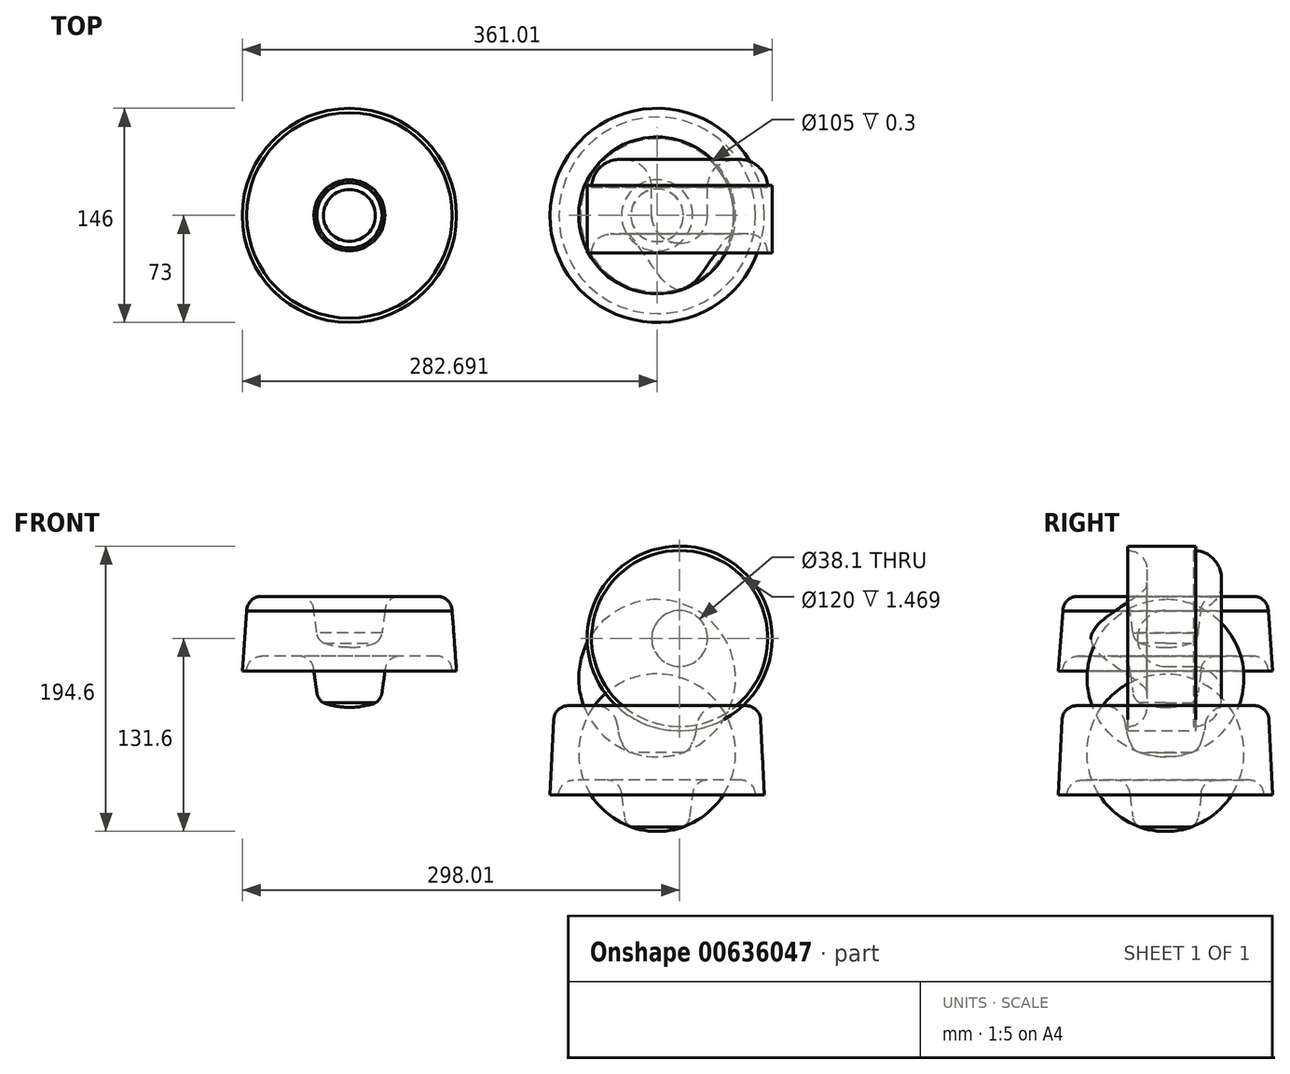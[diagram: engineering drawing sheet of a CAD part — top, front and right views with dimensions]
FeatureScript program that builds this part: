
annotation { "Feature Type Name" : "Feature", "Feature Type Description" : "" }
export const myFeature = defineFeature(function(context is Context, id is Id, definition is map)
    precondition{}
    {
        {
            var Q0;
            Q0=qCreatedBy(makeId("Top.planeOp"),FACE);
            var sketch = newSketch(context, id + "F0", { "sketchPlane" : qUnion([Q0])});
            skLineSegment(sketch, "E0", {"start": v(-19.05, 19.05) * mm, "end": v(19.05, 19.05) * mm, "construction": true});
            skPoint(sketch, "E1", {"position": v(0, 19.05) * mm});
            skLineSegment(sketch, "E2", {"start": v(19.05, 19.05) * mm, "end": v(19.05, 0) * mm});
            skLineSegment(sketch, "E3", {"start": v(-19.05, 19.05) * mm, "end": v(-19.05, 0) * mm});
            skArc(sketch, "E4", {"start": v(-19.05, 0) * mm, "mid": v(0, -19.05) * mm, "end": v(19.05, 0) * mm});
            skLineSegment(sketch, "E5", {"start": v(-19.05, 19.05) * mm, "end": v(-19.05, 19.05) * mm});
            skLineSegment(sketch, "E6", {"start": v(-38.1, 38.1) * mm, "end": v(-40.95, 38.1) * mm});
            skLineSegment(sketch, "E7", {"start": v(-60, 20.52) * mm, "end": v(-60, 19.05) * mm});
            skLineSegment(sketch, "E8", {"start": v(-60, 20.52) * mm, "end": v(-63, 20.52) * mm});
            skLineSegment(sketch, "E9", {"start": v(-63, 20.52) * mm, "end": v(-63, -25.7) * mm});
            skLineSegment(sketch, "E10", {"start": v(-63, -25.7) * mm, "end": v(-60, -25.7) * mm});
            skLineSegment(sketch, "E11", {"start": v(-60, -25.7) * mm, "end": v(-60, -25.7) * mm});
            skPoint(sketch, "E12.visualSharp", {"position": v(-60, 38.1) * mm});
            skArc(sketch, "E12.filletArc", {"start": v(-40.95, 38.1) * mm, "mid": v(-54.42, 32.52) * mm, "end": v(-60, 19.05) * mm});
            skPoint(sketch, "E13.visualSharp", {"position": v(-19.05, 38.1) * mm});
            skArc(sketch, "E13.filletArc", {"start": v(-19.05, 19.05) * mm, "mid": v(-24.63, 32.52) * mm, "end": v(-38.1, 38.1) * mm});
            skLineSegment(sketch, "E14", {"start": v(-47, -12.7) * mm, "end": v(-38.1, -12.7) * mm});
            skPoint(sketch, "E15.visualSharp", {"position": v(-60, -12.7) * mm});
            skArc(sketch, "E15.filletArc", {"start": v(-47, -12.7) * mm, "mid": v(-56.2, -16.5) * mm, "end": v(-60, -25.7) * mm});
            skLineSegment(sketch, "E16", {"start": v(0, 0) * mm, "end": v(0, -8.3) * mm, "construction": true});
            skLineSegment(sketch, "E17.MirrorCS", {"start": v(47, -12.7) * mm, "end": v(38.1, -12.7) * mm});
            skArc(sketch, "E18.MirrorCS", {"start": v(47, -12.7) * mm, "mid": v(56.2, -16.5) * mm, "end": v(60, -25.7) * mm});
            skLineSegment(sketch, "E19.MirrorCS", {"start": v(60, -25.7) * mm, "end": v(60, -25.7) * mm});
            skLineSegment(sketch, "E20.MirrorCS", {"start": v(63, -25.7) * mm, "end": v(60, -25.7) * mm});
            skLineSegment(sketch, "E21.MirrorCS", {"start": v(63, 20.52) * mm, "end": v(63, -25.7) * mm});
            skLineSegment(sketch, "E22.MirrorCS", {"start": v(60, 20.52) * mm, "end": v(63, 20.52) * mm});
            skArc(sketch, "E23.MirrorCS", {"start": v(40.95, 38.1) * mm, "mid": v(54.42, 32.52) * mm, "end": v(60, 19.05) * mm});
            skLineSegment(sketch, "E24.MirrorCS", {"start": v(38.1, 38.1) * mm, "end": v(40.95, 38.1) * mm});
            skArc(sketch, "E25.MirrorCS", {"start": v(19.05, 19.05) * mm, "mid": v(24.63, 32.52) * mm, "end": v(38.1, 38.1) * mm});
            skArc(sketch, "E26.MirrorCS", {"start": v(19.05, 0) * mm, "mid": v(0, -19.05) * mm, "end": v(-19.05, 0) * mm});
            skPoint(sketch, "E27.visualSharp", {"position": v(-26.3, -53.05) * mm});
            skFitSpline(sketch, "E28", {"points": [v(0, -50.8) * mm, v(-6.75, -48.08) * mm, v(-12.26, -43.09) * mm, v(-17.78, -35.73) * mm, v(-25.53, -24.43) * mm, v(-33.42, -14.18) * mm, v(-38.1, -12.7) * mm], "startDerivative": vector(-41.62, -2.2) * mm, "endDerivative": vector(-48.29, 0) * mm});
            skFitSpline(sketch, "E29.MirrorCS", {"points": [v(0, -50.8) * mm, v(6.75, -48.08) * mm, v(12.26, -43.09) * mm, v(17.78, -35.73) * mm, v(25.53, -24.43) * mm, v(33.42, -14.18) * mm, v(38.1, -12.7) * mm], "startDerivative": vector(41.62, -2.2) * mm, "endDerivative": vector(48.29, 0) * mm});
            skLineSegment(sketch, "E30", {"start": v(0, -50.8) * mm, "end": v(0, -19.05) * mm});
            skSolve(sketch);
        }
        {
            var Q0;
            Q0 = qSketchRegion(id + "F0", true);
            var Q1;
            Q1=sQuery(id+"F0.wireOp",EDGE,"E16");
            revolve(context, id + "F1", {"entities" : qUnion([Q0]), "axis" : qUnion([Q1]), "revolveType" : RevolveType.FULL});
        }
        {
            var Q0;
            Q0=qCreatedBy(makeId("Front.planeOp"),FACE);
            var sketch = newSketch(context, id + "F2", { "sketchPlane" : qUnion([Q0])});
            skLineSegment(sketch, "E31", {"start": v(-165.01, 28.7) * mm, "end": v(-190.81, 28.7) * mm});
            skLineSegment(sketch, "E32", {"start": v(-207.31, -3.16) * mm, "end": v(-242.71, -3.16) * mm, "construction": true});
            skLineSegment(sketch, "E33", {"start": v(-259.21, 28.7) * mm, "end": v(-285.01, 28.7) * mm});
            skLineSegment(sketch, "E34", {"start": v(-249.21, -22.1) * mm, "end": v(-249.21, -43.96) * mm, "construction": true});
            skLineSegment(sketch, "E35", {"start": v(-249.21, -43.96) * mm, "end": v(-200.81, -43.96) * mm, "construction": true});
            skLineSegment(sketch, "E36", {"start": v(-200.81, -43.96) * mm, "end": v(-200.81, -22.1) * mm, "construction": true});
            skLineSegment(sketch, "E37", {"start": v(-190.81, -12.1) * mm, "end": v(-165.01, -12.1) * mm});
            skLineSegment(sketch, "E38", {"start": v(-155.01, -22.1) * mm, "end": v(-155.01, -22.1) * mm});
            skLineSegment(sketch, "E39", {"start": v(-259.21, -12.1) * mm, "end": v(-285.01, -12.1) * mm});
            skLineSegment(sketch, "E40", {"start": v(-295.01, -22.1) * mm, "end": v(-295.01, -22.1) * mm});
            skPoint(sketch, "E41.visualSharp", {"position": v(-295.01, -12.1) * mm});
            skArc(sketch, "E41.filletArc", {"start": v(-285.01, -12.1) * mm, "mid": v(-292.08, -15.02) * mm, "end": v(-295.01, -22.1) * mm});
            skPoint(sketch, "E42.visualSharp", {"position": v(-155.01, -12.1) * mm});
            skArc(sketch, "E42.filletArc", {"start": v(-155.01, -22.1) * mm, "mid": v(-157.94, -15.02) * mm, "end": v(-165.01, -12.1) * mm});
            skPoint(sketch, "E43.visualSharp", {"position": v(-155.01, 28.7) * mm});
            skArc(sketch, "E43.filletArc", {"start": v(-155.01, 18.7) * mm, "mid": v(-157.94, 25.78) * mm, "end": v(-165.01, 28.7) * mm});
            skPoint(sketch, "E44.visualSharp", {"position": v(-200.81, 28.7) * mm});
            skArc(sketch, "E44.filletArc", {"start": v(-190.81, 28.7) * mm, "mid": v(-197.88, 25.78) * mm, "end": v(-200.81, 18.7) * mm});
            skPoint(sketch, "E45.visualSharp", {"position": v(-239.88, 28.7) * mm});
            skArc(sketch, "E45.filletArc", {"start": v(-249.21, 18.7) * mm, "mid": v(-252.14, 25.78) * mm, "end": v(-259.21, 28.7) * mm});
            skPoint(sketch, "E46.visualSharp", {"position": v(-295.01, 28.7) * mm});
            skArc(sketch, "E46.filletArc", {"start": v(-285.01, 28.7) * mm, "mid": v(-292.08, 25.78) * mm, "end": v(-295.01, 18.7) * mm});
            skPoint(sketch, "E47.visualSharp", {"position": v(-249.21, -12.1) * mm});
            skArc(sketch, "E47.filletArc", {"start": v(-249.21, -22.1) * mm, "mid": v(-252.14, -15.02) * mm, "end": v(-259.21, -12.1) * mm});
            skPoint(sketch, "E48.visualSharp", {"position": v(-200.81, -12.1) * mm});
            skArc(sketch, "E48.filletArc", {"start": v(-190.81, -12.1) * mm, "mid": v(-197.88, -15.02) * mm, "end": v(-200.81, -22.1) * mm});
            skArc(sketch, "E49", {"start": v(-242.71, -3.16) * mm, "mid": v(-225.01, -6.16) * mm, "end": v(-207.31, -3.16) * mm});
            skPoint(sketch, "E50", {"position": v(-225.01, -3.16) * mm});
            skPoint(sketch, "E51", {"position": v(-225.01, -43.96) * mm});
            skArc(sketch, "E52", {"start": v(-207.31, -3.16) * mm, "mid": v(-204.3, -0.15) * mm, "end": v(-202.81, 3.84) * mm});
            skArc(sketch, "E53", {"start": v(-247.21, 3.84) * mm, "mid": v(-245.73, -0.15) * mm, "end": v(-242.71, -3.16) * mm});
            skLineSegment(sketch, "E54", {"start": v(-247.21, 3.84) * mm, "end": v(-202.81, 3.84) * mm, "construction": true});
            skPoint(sketch, "E55", {"position": v(-225.01, 3.84) * mm});
            skFitSpline(sketch, "E56", {"points": [v(-200.81, 18.7) * mm, v(-201.81, 11.64) * mm, v(-202.81, 3.84) * mm], "startDerivative": vector(-1.39, -14.42) * mm, "endDerivative": vector(-2.6, -15.3) * mm});
            skFitSpline(sketch, "E57", {"points": [v(-249.21, 18.7) * mm, v(-248.21, 11.64) * mm, v(-247.21, 3.84) * mm], "startDerivative": vector(1.62, -14.4) * mm, "endDerivative": vector(2.37, -15.31) * mm});
            skLineSegment(sketch, "E58", {"start": v(-248.21, 11.64) * mm, "end": v(-201.81, 11.64) * mm, "construction": true});
            skPoint(sketch, "E59", {"position": v(-225.01, 11.64) * mm});
            skArc(sketch, "E60", {"start": v(-242.71, -43.96) * mm, "mid": v(-233.99, -46.2) * mm, "end": v(-225.01, -46.96) * mm});
            skArc(sketch, "E61", {"start": v(-207.31, -43.96) * mm, "mid": v(-204.3, -40.95) * mm, "end": v(-202.81, -36.96) * mm});
            skArc(sketch, "E62", {"start": v(-247.21, -36.96) * mm, "mid": v(-245.73, -40.95) * mm, "end": v(-242.71, -43.96) * mm});
            skFitSpline(sketch, "E63", {"points": [v(-247.21, -36.96) * mm, v(-248.3, -29.16) * mm, v(-249.21, -22.1) * mm], "startDerivative": vector(-2.29, 16.5) * mm, "endDerivative": vector(-1.71, 17.13) * mm});
            skFitSpline(sketch, "E64", {"points": [v(-202.81, -36.96) * mm, v(-201.9, -29.16) * mm, v(-200.81, -22.1) * mm], "startDerivative": vector(1.97, 16.43) * mm, "endDerivative": vector(2.03, 16.5) * mm});
            skLineSegment(sketch, "E65", {"start": v(-247.21, -36.96) * mm, "end": v(-202.81, -36.96) * mm, "construction": true});
            skLineSegment(sketch, "E66", {"start": v(-248.3, -29.16) * mm, "end": v(-201.9, -29.16) * mm, "construction": true});
            skPoint(sketch, "E67", {"position": v(-225.1, -29.16) * mm});
            skPoint(sketch, "E68", {"position": v(-225.01, -36.96) * mm});
            skLineSegment(sketch, "E69", {"start": v(-155.01, 18.7) * mm, "end": v(-152.01, -22.1) * mm});
            skLineSegment(sketch, "E70", {"start": v(-295.01, 18.7) * mm, "end": v(-298.01, -22.1) * mm});
            skPoint(sketch, "E71.end.orphan", {"position": v(-155.01, -22.1) * mm});
            skPoint(sketch, "E72.start.orphan", {"position": v(-295.01, -22.1) * mm});
            skLineSegment(sketch, "E73", {"start": v(-295.01, -22.1) * mm, "end": v(-298.01, -22.1) * mm});
            skLineSegment(sketch, "E74", {"start": v(-155.01, -22.1) * mm, "end": v(-152.01, -22.1) * mm});
            skLineSegment(sketch, "E75", {"start": v(-225.01, 3.84) * mm, "end": v(-225.01, -43.96) * mm, "construction": true});
            skLineSegment(sketch, "E76", {"start": v(-225.01, -6.16) * mm, "end": v(-225.01, -46.96) * mm});
            skSolve(sketch);
        }
        {
            var Q0;
            {var subQ0=sQuery(id+"F2.wireOp",EDGE,"E60");Q0=makeQuery(id+"F2.imprint","IMPRINT",FACE,{"disambiguationData":[TD([[makeQuery(id+"F2.imprint","IMPRINT",EDGE,{"derivedFrom":subQ0}),1.0]])]});}
            var Q1;
            Q1=makeQuery(id+"F2.imprint","IMPRINT",FACE,{"disambiguationData":[TD([[makeQuery(id+"F2.imprint","IMPRINT",EDGE,{"derivedFrom":sQuery(id+"F2.wireOp",EDGE,"E31")}),1.0]])]});
            var Q2;
            Q2=sQuery(id+"F2.wireOp",EDGE,"E76");
            revolve(context, id + "F3", {"entities" : qUnion([Q0, Q1]), "axis" : qUnion([Q2]), "revolveType" : RevolveType.FULL});
        }
        {
            var Q0;
            Q0=qCreatedBy(makeId("Front.planeOp"),FACE);
            var sketch = newSketch(context, id + "F4", { "sketchPlane" : qUnion([Q0])});
            skLineSegment(sketch, "E77", {"start": v(44.68, 58.67) * mm, "end": v(18.88, 58.67) * mm});
            skLineSegment(sketch, "E78", {"start": v(2.38, 26.67) * mm, "end": v(-33.02, 26.67) * mm, "construction": true});
            skLineSegment(sketch, "E79", {"start": v(-39.52, 7.87) * mm, "end": v(-39.52, -14.13) * mm, "construction": true});
            skLineSegment(sketch, "E80", {"start": v(-39.52, -14.13) * mm, "end": v(8.88, -14.13) * mm, "construction": true});
            skLineSegment(sketch, "E81", {"start": v(8.88, -14.13) * mm, "end": v(8.88, 7.87) * mm, "construction": true});
            skLineSegment(sketch, "E82", {"start": v(18.88, 17.87) * mm, "end": v(44.68, 17.87) * mm});
            skLineSegment(sketch, "E83", {"start": v(54.68, 7.87) * mm, "end": v(54.68, 7.87) * mm});
            skLineSegment(sketch, "E84", {"start": v(-49.52, 17.87) * mm, "end": v(-75.32, 17.87) * mm});
            skLineSegment(sketch, "E85", {"start": v(-85.32, 7.87) * mm, "end": v(-85.32, 7.87) * mm});
            skPoint(sketch, "E86.visualSharp", {"position": v(-85.32, 17.87) * mm});
            skArc(sketch, "E86.filletArc", {"start": v(-75.32, 17.87) * mm, "mid": v(-82.4, 14.94) * mm, "end": v(-85.32, 7.87) * mm});
            skPoint(sketch, "E87.visualSharp", {"position": v(54.68, 17.87) * mm});
            skArc(sketch, "E87.filletArc", {"start": v(54.68, 7.87) * mm, "mid": v(51.75, 14.94) * mm, "end": v(44.68, 17.87) * mm});
            skPoint(sketch, "E88.visualSharp", {"position": v(54.68, 58.67) * mm});
            skArc(sketch, "E88.filletArc", {"start": v(54.68, 48.67) * mm, "mid": v(51.75, 55.74) * mm, "end": v(44.68, 58.67) * mm});
            skPoint(sketch, "E89.visualSharp", {"position": v(8.88, 58.67) * mm});
            skArc(sketch, "E89.filletArc", {"start": v(18.88, 58.67) * mm, "mid": v(11.8, 55.74) * mm, "end": v(8.88, 48.67) * mm});
            skPoint(sketch, "E90.visualSharp", {"position": v(-30.18, 58.67) * mm});
            skArc(sketch, "E90.filletArc", {"start": v(-39.52, 48.67) * mm, "mid": v(-42.45, 55.74) * mm, "end": v(-49.52, 58.67) * mm});
            skPoint(sketch, "E91.visualSharp", {"position": v(-85.32, 58.67) * mm});
            skArc(sketch, "E91.filletArc", {"start": v(-75.32, 58.67) * mm, "mid": v(-82.4, 55.74) * mm, "end": v(-85.32, 48.67) * mm});
            skPoint(sketch, "E92.visualSharp", {"position": v(-39.52, 17.87) * mm});
            skArc(sketch, "E92.filletArc", {"start": v(-39.52, 7.87) * mm, "mid": v(-42.45, 14.94) * mm, "end": v(-49.52, 17.87) * mm});
            skPoint(sketch, "E93.visualSharp", {"position": v(8.88, 17.87) * mm});
            skArc(sketch, "E93.filletArc", {"start": v(18.88, 17.87) * mm, "mid": v(11.8, 14.94) * mm, "end": v(8.88, 7.87) * mm});
            skArc(sketch, "E94", {"start": v(-33.02, 26.67) * mm, "mid": v(-24.3, 24.43) * mm, "end": v(-15.32, 23.67) * mm});
            skPoint(sketch, "E95", {"position": v(-15.32, 26.67) * mm});
            skPoint(sketch, "E96", {"position": v(-15.32, -14.13) * mm});
            skArc(sketch, "E97", {"start": v(2.38, 26.67) * mm, "mid": v(5.4, 29.68) * mm, "end": v(6.88, 33.67) * mm});
            skArc(sketch, "E98", {"start": v(-37.52, 33.67) * mm, "mid": v(-36.03, 29.68) * mm, "end": v(-33.02, 26.67) * mm});
            skLineSegment(sketch, "E99", {"start": v(-37.52, 33.67) * mm, "end": v(6.88, 33.67) * mm, "construction": true});
            skPoint(sketch, "E100", {"position": v(-15.32, 33.67) * mm});
            skFitSpline(sketch, "E101", {"points": [v(8.88, 48.67) * mm, v(7.88, 41.47) * mm, v(6.88, 33.67) * mm], "startDerivative": vector(-1.39, -14.42) * mm, "endDerivative": vector(-2.6, -15.3) * mm});
            skFitSpline(sketch, "E102", {"points": [v(-39.52, 48.67) * mm, v(-38.52, 41.47) * mm, v(-37.52, 33.67) * mm], "startDerivative": vector(1.62, -14.4) * mm, "endDerivative": vector(2.37, -15.31) * mm});
            skLineSegment(sketch, "E103", {"start": v(-38.52, 41.47) * mm, "end": v(7.88, 41.47) * mm, "construction": true});
            skPoint(sketch, "E104", {"position": v(-15.32, 41.47) * mm});
            skArc(sketch, "E105", {"start": v(-33.02, -14.13) * mm, "mid": v(-24.3, -16.37) * mm, "end": v(-15.32, -17.13) * mm});
            skArc(sketch, "E106", {"start": v(2.38, -14.13) * mm, "mid": v(5.4, -11.12) * mm, "end": v(6.88, -7.13) * mm});
            skArc(sketch, "E107", {"start": v(-37.52, -7.13) * mm, "mid": v(-36.03, -11.12) * mm, "end": v(-33.02, -14.13) * mm});
            skFitSpline(sketch, "E108", {"points": [v(-37.52, -7.13) * mm, v(-38.6, 0.67) * mm, v(-39.52, 7.87) * mm], "startDerivative": vector(-2.29, 16.5) * mm, "endDerivative": vector(-1.71, 17.13) * mm});
            skFitSpline(sketch, "E109", {"points": [v(6.88, -7.13) * mm, v(7.8, 0.67) * mm, v(8.88, 7.87) * mm], "startDerivative": vector(1.97, 16.43) * mm, "endDerivative": vector(2.03, 16.5) * mm});
            skLineSegment(sketch, "E110", {"start": v(-37.52, -7.13) * mm, "end": v(6.88, -7.13) * mm, "construction": true});
            skLineSegment(sketch, "E111", {"start": v(-38.6, 0.67) * mm, "end": v(7.8, 0.67) * mm, "construction": true});
            skPoint(sketch, "E112", {"position": v(-15.4, 0.67) * mm});
            skPoint(sketch, "E113", {"position": v(-15.32, -7.13) * mm});
            skLineSegment(sketch, "E114", {"start": v(54.68, 48.67) * mm, "end": v(57.68, 7.87) * mm});
            skLineSegment(sketch, "E115", {"start": v(-85.32, 48.67) * mm, "end": v(-88.32, 7.87) * mm});
            skPoint(sketch, "E116.end.orphan", {"position": v(54.68, 7.87) * mm});
            skPoint(sketch, "E117.start.orphan", {"position": v(-85.32, 7.87) * mm});
            skLineSegment(sketch, "E118", {"start": v(-85.32, 7.87) * mm, "end": v(-88.32, 7.87) * mm});
            skLineSegment(sketch, "E119", {"start": v(54.68, 7.87) * mm, "end": v(57.68, 7.87) * mm});
            skLineSegment(sketch, "E120", {"start": v(-15.32, 33.67) * mm, "end": v(-15.32, -14.13) * mm, "construction": true});
            skLineSegment(sketch, "E121", {"start": v(-15.32, 23.67) * mm, "end": v(-15.32, -17.13) * mm});
            skLineSegment(sketch, "E122", {"start": v(-15.32, -80.8) * mm, "end": v(-15.32, -131.6) * mm});
            skLineSegment(sketch, "E123", {"start": v(-15.32, -80.8) * mm, "end": v(-42.32, -80.8) * mm, "construction": true});
            skLineSegment(sketch, "E124", {"start": v(-42.32, -80.8) * mm, "end": v(-42.32, -60.8) * mm, "construction": true});
            skLineSegment(sketch, "E125", {"start": v(-42.32, -60.8) * mm, "end": v(-42.32, -60.8) * mm});
            skLineSegment(sketch, "E126", {"start": v(-57.32, -45.8) * mm, "end": v(-57.32, -45.8) * mm});
            skLineSegment(sketch, "E127", {"start": v(-57.32, -45.8) * mm, "end": v(-75.8, -45.8) * mm});
            skLineSegment(sketch, "E128", {"start": v(-85.32, -45.8) * mm, "end": v(-85.32, -106.6) * mm, "construction": true});
            skLineSegment(sketch, "E129", {"start": v(-85.32, -106.6) * mm, "end": v(-88.32, -106.6) * mm});
            skLineSegment(sketch, "E130", {"start": v(-88.32, -106.6) * mm, "end": v(-85.79, -55.3) * mm});
            skLineSegment(sketch, "E131", {"start": v(-85.32, -106.6) * mm, "end": v(-82.32, -106.6) * mm});
            skLineSegment(sketch, "E132", {"start": v(-82.32, -106.6) * mm, "end": v(-82.32, -106.6) * mm});
            skLineSegment(sketch, "E133", {"start": v(-72.32, -96.6) * mm, "end": v(-72.32, -96.6) * mm});
            skLineSegment(sketch, "E134", {"start": v(-72.32, -96.6) * mm, "end": v(-49.52, -96.6) * mm});
            skLineSegment(sketch, "E135", {"start": v(-49.52, -96.6) * mm, "end": v(-49.52, -96.6) * mm});
            skLineSegment(sketch, "E136", {"start": v(-39.52, -106.6) * mm, "end": v(-39.52, -106.6) * mm});
            skPoint(sketch, "E137.visualSharp", {"position": v(-85.32, -45.8) * mm});
            skArc(sketch, "E137.filletArc", {"start": v(-75.8, -45.8) * mm, "mid": v(-82.7, -48.56) * mm, "end": v(-85.79, -55.3) * mm});
            skPoint(sketch, "E138.visualSharp", {"position": v(-42.32, -45.8) * mm});
            skArc(sketch, "E138.filletArc", {"start": v(-42.32, -60.8) * mm, "mid": v(-46.71, -50.2) * mm, "end": v(-57.32, -45.8) * mm});
            skPoint(sketch, "E139.visualSharp", {"position": v(-82.32, -96.6) * mm});
            skArc(sketch, "E139.filletArc", {"start": v(-72.32, -96.6) * mm, "mid": v(-79.4, -99.53) * mm, "end": v(-82.32, -106.6) * mm});
            skPoint(sketch, "E140.visualSharp", {"position": v(-39.52, -96.6) * mm});
            skArc(sketch, "E140.filletArc", {"start": v(-39.52, -106.6) * mm, "mid": v(-42.45, -99.53) * mm, "end": v(-49.52, -96.6) * mm});
            skArc(sketch, "E141", {"start": v(-33.13, -128.66) * mm, "mid": v(-24.35, -130.88) * mm, "end": v(-15.32, -131.6) * mm});
            skArc(sketch, "E142", {"start": v(-37.63, -121.66) * mm, "mid": v(-36.14, -125.65) * mm, "end": v(-33.13, -128.66) * mm});
            skFitSpline(sketch, "E143", {"points": [v(-37.63, -121.66) * mm, v(-38.72, -113.86) * mm, v(-39.52, -106.6) * mm], "startDerivative": vector(-2.29, 16.5) * mm, "endDerivative": vector(-1.71, 17.13) * mm});
            skArc(sketch, "E144", {"start": v(-33.25, -77.82) * mm, "mid": v(-24.4, -80.07) * mm, "end": v(-15.32, -80.8) * mm});
            skArc(sketch, "E145", {"start": v(-39.14, -71.49) * mm, "mid": v(-36.91, -75.32) * mm, "end": v(-33.25, -77.82) * mm});
            skFitSpline(sketch, "E146", {"points": [v(-42.32, -60.8) * mm, v(-40.95, -66.64) * mm, v(-39.14, -71.49) * mm], "startDerivative": vector(3.52, -10.99) * mm, "endDerivative": vector(4.83, -11.27) * mm});
            skSolve(sketch);
        }
        {
            var Q0;
            Q0=makeQuery(id+"F4.imprint","IMPRINT",FACE,{"disambiguationData":[TD([[makeQuery(id+"F4.imprint","IMPRINT",EDGE,{"derivedFrom":sQuery(id+"F4.wireOp",EDGE,"E122")}),-1.0]])]});
            var Q1;
            Q1=sQuery(id+"F4.wireOp",EDGE,"E122");
            revolve(context, id + "F5", {"entities" : qUnion([Q0]), "axis" : qUnion([Q1]), "revolveType" : RevolveType.FULL});
        }
        {
            var Q0;
            Q0=makeQuery(id+"F5.opRevolve","SWEPT_EDGE",EDGE,{"disambiguationData":[OSD([sQuery(id+"F4.wireOp",EDGE,"E138.filletArc"),sQuery(id+"F4.wireOp",EDGE,"E146")])]});
            var Q1;
            Q1=makeQuery(id+"F5.opRevolve","SWEPT_EDGE",EDGE,{"disambiguationData":[OSD([sQuery(id+"F4.wireOp",EDGE,"E145"),sQuery(id+"F4.wireOp",EDGE,"E146")])]});
            fillet(context, id + "F6", {"entities" : qUnion([Q0, Q1]), "radius" : 25 * mm, "tangentPropagation" : true, "allowEdgeOverflow" : false});
        }
        {
            var Q0;
            Q0=makeQuery(id+"F5.opRevolve","SWEPT_FACE",FACE,{"disambiguationData":[OSD([sQuery(id+"F4.wireOp",EDGE,"E127")])]});
            var sketch = newSketch(context, id + "F7", { "sketchPlane" : qUnion([Q0])});
            skCircle(sketch, "E147", {"center": v(-15.32, 0) * mm, "radius": 52.5 * mm});
            skCircle(sketch, "E148", {"center": v(-15.32, 0) * mm, "radius": 52.2 * mm});
            skSolve(sketch);
        }
        {
            var Q0;
            Q0 = qSketchRegion(id + "F7", true);
            extrude(context, id + "F8", {"entities" : qUnion([Q0]), "operationType" : NewBodyOperationType.REMOVE, "oppositeDirection" : true, "depth" : .3 * mm, "offsetDistance" : 25 * mm});
        }
    });
